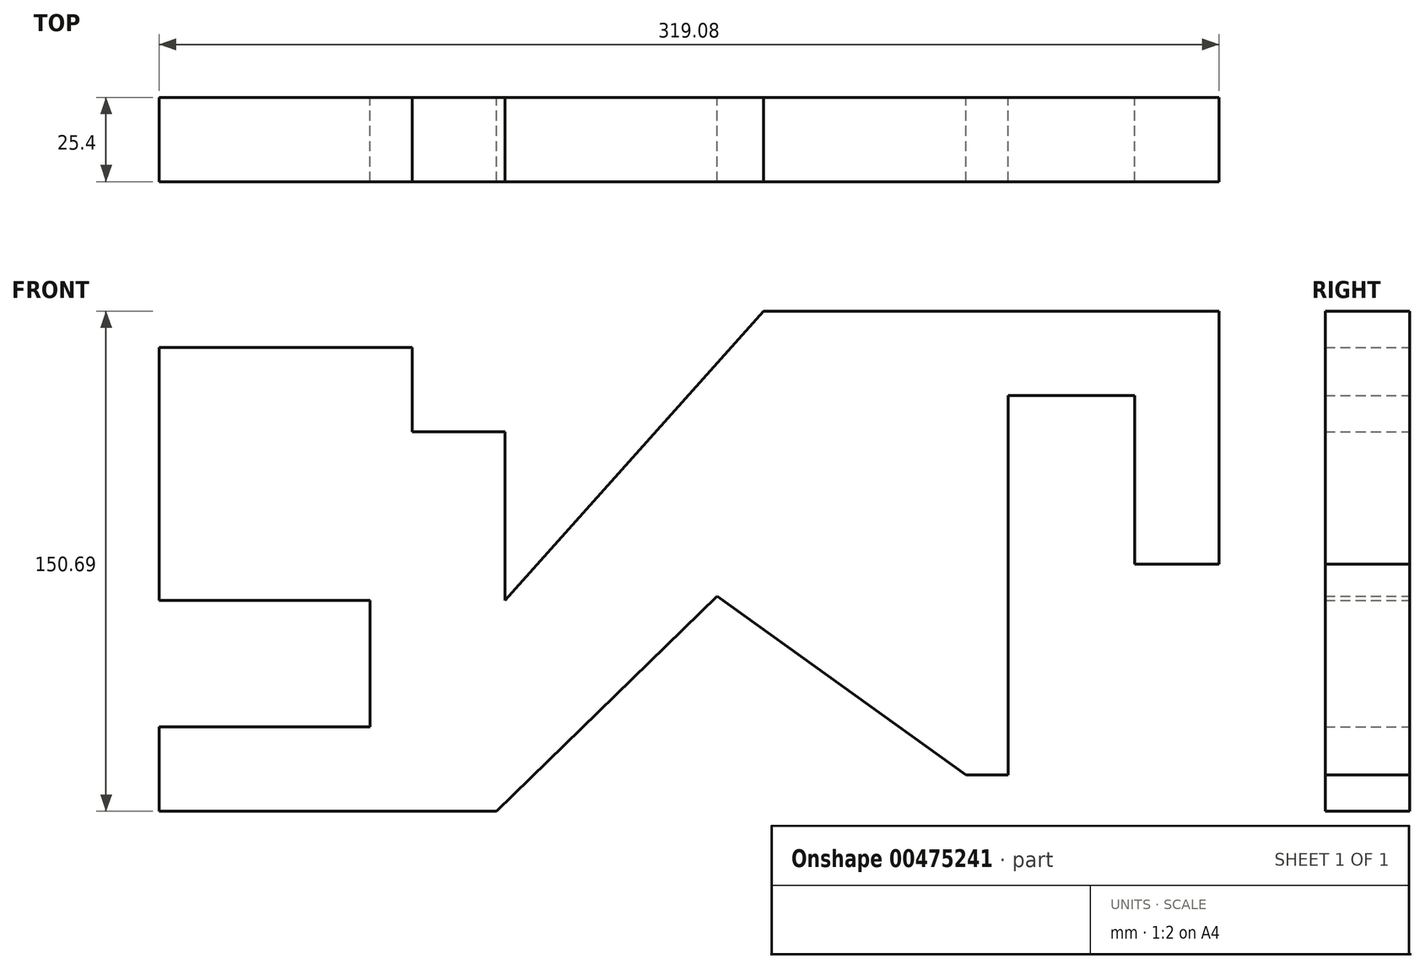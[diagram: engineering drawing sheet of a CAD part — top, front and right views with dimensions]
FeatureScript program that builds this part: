
annotation { "Feature Type Name" : "Feature", "Feature Type Description" : "" }
export const myFeature = defineFeature(function(context is Context, id is Id, definition is map)
    precondition{}
    {
        {
            var Q0;
            Q0=qCreatedBy(makeId("Front.planeOp"),FACE);
            var sketch = newSketch(context, id + "F0", { "sketchPlane" : qUnion([Q0])});
            skLineSegment(sketch, "E0", {"start": v(-104.14, 56.66) * mm, "end": v(-27.94, 56.66) * mm});
            skLineSegment(sketch, "E1", {"start": v(-27.94, 56.66) * mm, "end": v(-27.94, 31.26) * mm});
            skLineSegment(sketch, "E2", {"start": v(-27.94, 31.26) * mm, "end": v(0, 31.26) * mm});
            skLineSegment(sketch, "E3", {"start": v(-104.14, 56.66) * mm, "end": v(-104.14, -19.54) * mm});
            skLineSegment(sketch, "E4", {"start": v(-104.14, -19.54) * mm, "end": v(-40.64, -19.54) * mm});
            skLineSegment(sketch, "E5", {"start": v(-40.64, -19.54) * mm, "end": v(-40.64, -57.64) * mm});
            skLineSegment(sketch, "E6", {"start": v(-40.64, -57.64) * mm, "end": v(-104.14, -57.64) * mm});
            skLineSegment(sketch, "E7", {"start": v(-104.14, -57.64) * mm, "end": v(-104.14, -83.04) * mm});
            skLineSegment(sketch, "E8", {"start": v(-104.14, -83.04) * mm, "end": v(-2.54, -83.04) * mm});
            skPoint(sketch, "E9.end.orphan", {"position": v(75.79, -83.04) * mm});
            skLineSegment(sketch, "E10", {"start": v(-2.54, -83.04) * mm, "end": v(63.82, -18.25) * mm});
            skLineSegment(sketch, "E11", {"start": v(63.82, -18.25) * mm, "end": v(138.74, -72.05) * mm});
            skPoint(sketch, "E12.end.orphan", {"position": v(138.74, -74.57) * mm});
            skLineSegment(sketch, "E13", {"start": v(138.74, -72.05) * mm, "end": v(151.44, -72.05) * mm});
            skLineSegment(sketch, "E14", {"start": v(151.44, -72.05) * mm, "end": v(151.44, 42.25) * mm});
            skLineSegment(sketch, "E15", {"start": v(151.44, 42.25) * mm, "end": v(189.54, 42.25) * mm});
            skLineSegment(sketch, "E16", {"start": v(189.54, 42.25) * mm, "end": v(189.54, -8.55) * mm});
            skLineSegment(sketch, "E17", {"start": v(189.54, -8.55) * mm, "end": v(214.94, -8.55) * mm});
            skLineSegment(sketch, "E18", {"start": v(214.94, -8.55) * mm, "end": v(214.94, 67.65) * mm});
            skLineSegment(sketch, "E19", {"start": v(214.94, 67.65) * mm, "end": v(77.78, 67.65) * mm});
            skLineSegment(sketch, "E20", {"start": v(0, 31.26) * mm, "end": v(0, -19.54) * mm});
            skLineSegment(sketch, "E21", {"start": v(0, -19.54) * mm, "end": v(77.78, 67.65) * mm});
            skSolve(sketch);
        }
        {
            var Q0;
            Q0 = qSketchRegion(id + "F0", true);
            extrude(context, id + "F1", {"entities" : qUnion([Q0]), "depth" : 25.4 * mm});
        }
    });
